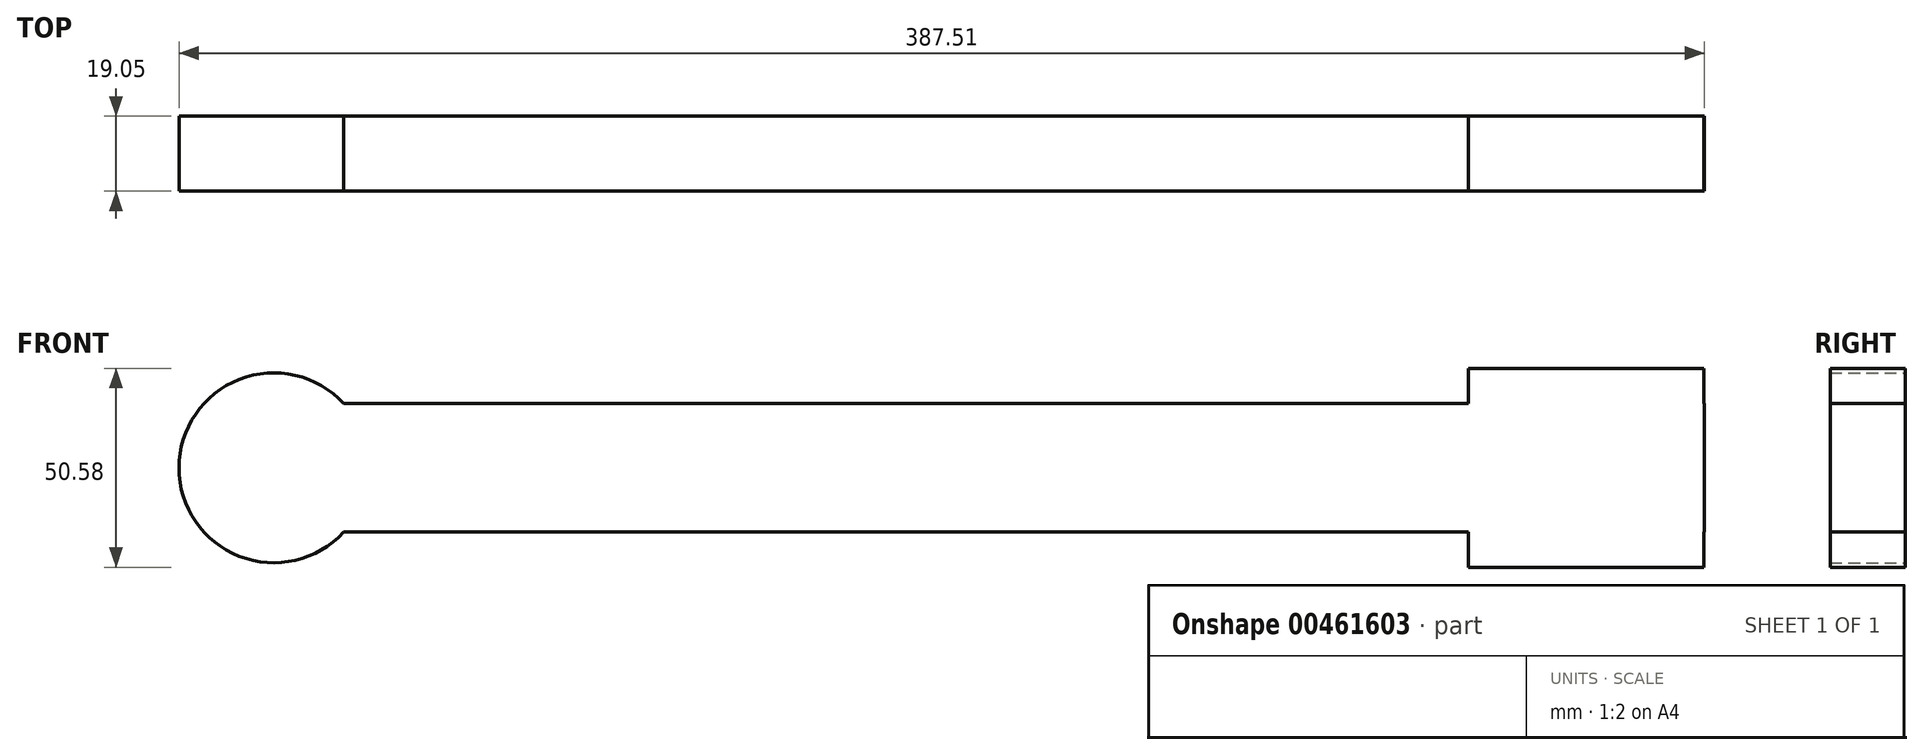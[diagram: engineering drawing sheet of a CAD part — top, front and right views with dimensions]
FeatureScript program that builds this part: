
annotation { "Feature Type Name" : "Feature", "Feature Type Description" : "" }
export const myFeature = defineFeature(function(context is Context, id is Id, definition is map)
    precondition{}
    {
        {
            var Q0;
            Q0=qCreatedBy(makeId("Front.planeOp"),FACE);
            var sketch = newSketch(context, id + "F0", { "sketchPlane" : qUnion([Q0])});
            skLineSegment(sketch, "E0.bottom", {"start": v(-181.28, 16.35) * mm, "end": v(181.28, 16.35) * mm});
            skLineSegment(sketch, "E0.top", {"start": v(-181.28, -16.35) * mm, "end": v(181.28, -16.35) * mm});
            skLineSegment(sketch, "E0.left", {"start": v(-181.28, 16.35) * mm, "end": v(-181.28, -16.35) * mm});
            skLineSegment(sketch, "E0.right", {"start": v(181.28, 16.35) * mm, "end": v(181.28, -16.35) * mm});
            skPoint(sketch, "E0.middle", {"position": v(0, 0) * mm});
            skSolve(sketch);
        }
        {
            var Q0;
            Q0=makeQuery(id+"F0.imprint","IMPRINT",FACE,{"disambiguationData":[TD([[makeQuery(id+"F0.imprint","IMPRINT",EDGE,{"derivedFrom":sQuery(id+"F0.wireOp",EDGE,"E0.bottom")}),-1.0]])]});
            var sketch = newSketch(context, id + "F1", { "sketchPlane" : qUnion([Q0])});
            skCircle(sketch, "E1", {"center": v(-182.11, 0) * mm, "radius": 24.12 * mm});
            skLineSegment(sketch, "E2.bottom", {"start": v(181.15, 25.3) * mm, "end": v(121.4, 25.3) * mm});
            skLineSegment(sketch, "E2.top", {"start": v(181.15, -25.3) * mm, "end": v(121.4, -25.3) * mm});
            skLineSegment(sketch, "E2.left", {"start": v(181.15, 25.3) * mm, "end": v(181.15, -25.3) * mm});
            skLineSegment(sketch, "E2.right", {"start": v(121.4, 25.3) * mm, "end": v(121.4, -25.3) * mm});
            skPoint(sketch, "E2.middle", {"position": v(151.28, 0) * mm});
            skSolve(sketch);
        }
        {
            var Q0;
            Q0 = qSketchRegion(id + "F0", true);
            var Q1;
            Q1 = qSketchRegion(id + "F1", true);
            extrude(context, id + "F2", {"entities" : qUnion([Q0, Q1]), "depth" : 19.05 * mm});
        }
        {
            var Q0;
            Q0=makeQuery(id+"F2.opExtrude","SWEPT_BODY",BODY,{"disambiguationData":[OSD([sQuery(id+"F1.wireOp",EDGE,"E2.bottom"),sQuery(id+"F1.wireOp",EDGE,"E2.top"),sQuery(id+"F1.wireOp",EDGE,"E2.left"),sQuery(id+"F1.wireOp",EDGE,"E2.right")])]});
            var Q1;
            Q1=makeQuery(id+"F2.opExtrude","SWEPT_BODY",BODY,{"disambiguationData":[OSD([sQuery(id+"F1.wireOp",EDGE,"E1")])]});
            var Q2;
            Q2=makeQuery(id+"F2.opExtrude","SWEPT_BODY",BODY,{"disambiguationData":[OSD([sQuery(id+"F0.wireOp",EDGE,"E0.bottom"),sQuery(id+"F0.wireOp",EDGE,"E0.top"),sQuery(id+"F0.wireOp",EDGE,"E0.left"),sQuery(id+"F0.wireOp",EDGE,"E0.right")])]});
            booleanBodies(context, id + "F3", {"operationType" : BooleanOperationType.UNION, "tools" : qUnion([Q0, Q1, Q2])});
        }
    });
